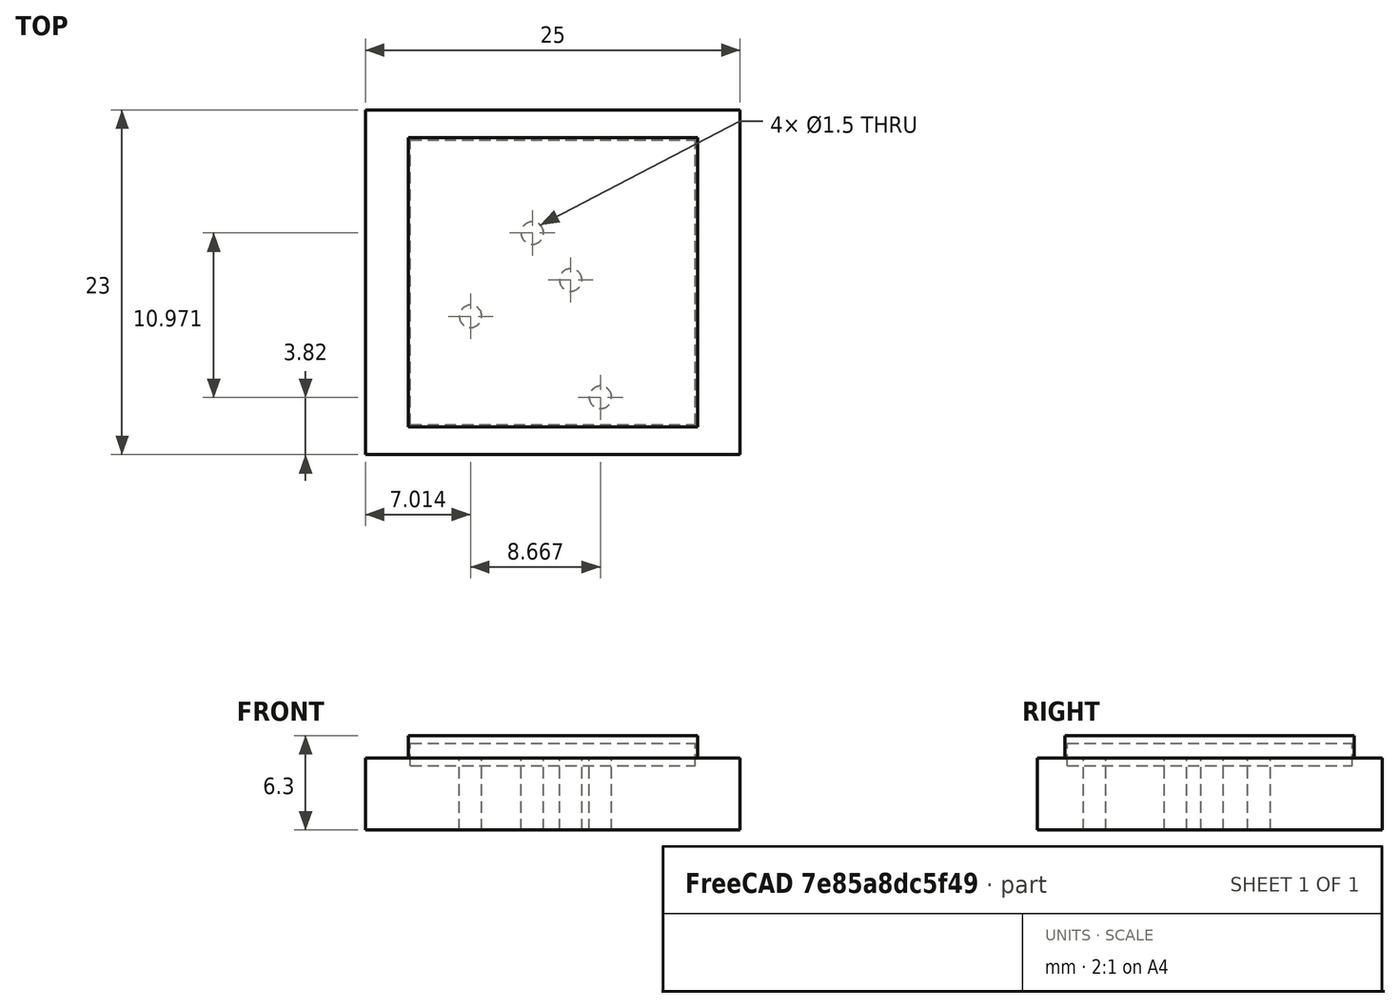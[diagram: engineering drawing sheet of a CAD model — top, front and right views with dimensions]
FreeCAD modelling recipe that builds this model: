
FCSTD DOCUMENT  (FreeCAD 0.18.4R)
Label: Soldering Jig
License: All rights reserved
LicenseURL: http://en.wikipedia.org/wiki/All_rights_reserved
objects: Part::Cylinder×4, Part::Box×3, Part::MultiFuse×1, Part::Cut×1, Part::Feature×1
note: 10 computed .brp shape members not serialized (recipe doc carries the construction recipe); baked Part::Feature solids carry a one-line shape summary decoded from their .brp

FEATURE [Part::Box] Box  label="Board"
  AttacherType = Attacher::AttachEngine3D
  Height = 1.5
  Length = 19
  Placement = pos=(0,0,5.5) rot=(0,0,1;0rad)
  Width = 19
FEATURE [Part::Cylinder] Cylinder
  Angle = 360
  AttacherType = Attacher::AttachEngine3D
  Height = 5.8
  Placement = pos=(8.137,12.791,1.2) rot=(0,0,1;0rad)
  Radius = 0.75
FEATURE [Part::Cylinder] Cylinder001
  Angle = 360
  AttacherType = Attacher::AttachEngine3D
  Height = 5.8
  Placement = pos=(10.694,9.658,1.2) rot=(0,0,1;0rad)
  Radius = 0.75
FEATURE [Part::Cylinder] Cylinder002
  Angle = 360
  AttacherType = Attacher::AttachEngine3D
  Height = 5.8
  Placement = pos=(4.014,7.228,1.2) rot=(0,0,1;0rad)
  Radius = 0.75
FEATURE [Part::Cylinder] Cylinder003
  Angle = 360
  AttacherType = Attacher::AttachEngine3D
  Height = 5.8
  Placement = pos=(12.681,1.82,1.2) rot=(0,0,1;0rad)
  Radius = 0.75
FEATURE [Part::Box] Box001  label="Board Hole"
  AttacherType = Attacher::AttachEngine3D
  Height = 1.5
  Length = 19.3
  Placement = pos=(-0.15,-0.15,6) rot=(0,0,1;0rad)
  Width = 19.3
FEATURE [Part::Box] Box002  label="Cube"
  AttacherType = Attacher::AttachEngine3D
  Height = 4.8
  Length = 25
  Placement = pos=(-3,-2,1.2) rot=(0,0,1;0rad)
  Width = 23
FEATURE [Part::MultiFuse] Fusion
  Shapes = -> [Cylinder,Cylinder003,Cylinder001,Cylinder002]
FEATURE [Part::Cut] Cut
  Base = -> Box002
  Tool = -> Fusion
FEATURE [Part::Feature] Cut_cs
  shape: bbox 25 x 23 x 3e-07 mm, 0 faces, 0 solids (baked)
